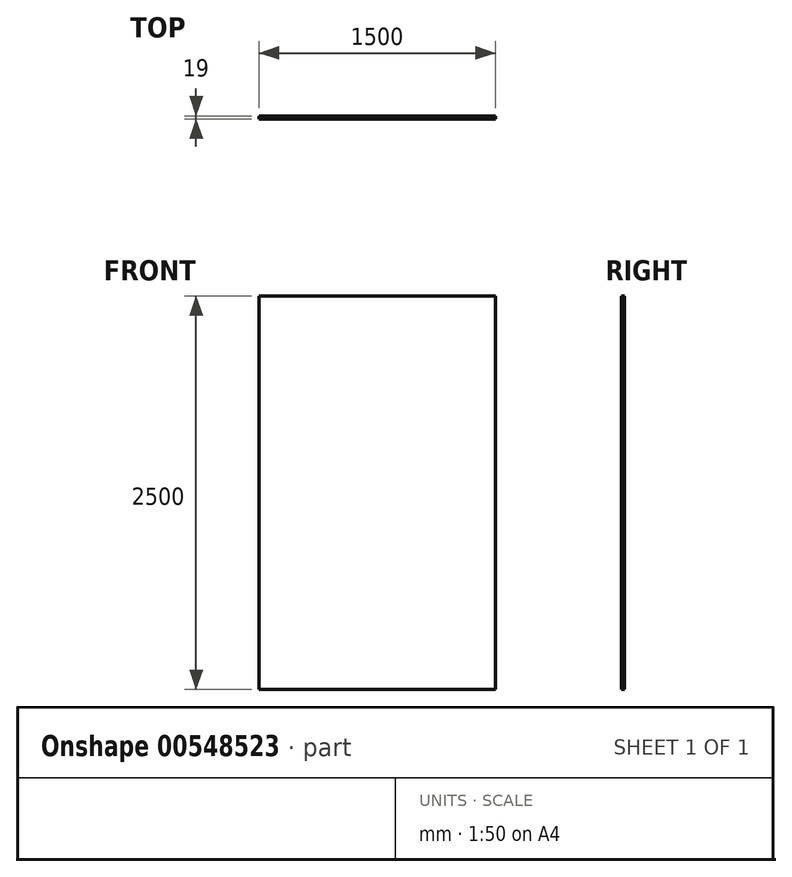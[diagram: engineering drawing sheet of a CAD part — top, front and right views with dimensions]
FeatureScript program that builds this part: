
annotation { "Feature Type Name" : "Feature", "Feature Type Description" : "" }
export const myFeature = defineFeature(function(context is Context, id is Id, definition is map)
    precondition{}
    {
        {
            var Q0;
            Q0=qCreatedBy(makeId("Front.planeOp"),FACE);
            var sketch = newSketch(context, id + "F0", { "sketchPlane" : qUnion([Q0])});
            skLineSegment(sketch, "E0.bottom", {"start": v(0, 0) * mm, "end": v(1500, 0) * mm});
            skLineSegment(sketch, "E0.top", {"start": v(0, 2500) * mm, "end": v(1500, 2500) * mm});
            skLineSegment(sketch, "E0.left", {"start": v(0, 0) * mm, "end": v(0, 2500) * mm});
            skLineSegment(sketch, "E0.right", {"start": v(1500, 0) * mm, "end": v(1500, 2500) * mm});
            skSolve(sketch);
        }
        {
            var Q0;
            Q0 = qSketchRegion(id + "F0", true);
            extrude(context, id + "F1", {"entities" : qUnion([Q0]), "depth" : 19 * mm, "offsetDistance" : 25 * mm});
        }
    });
